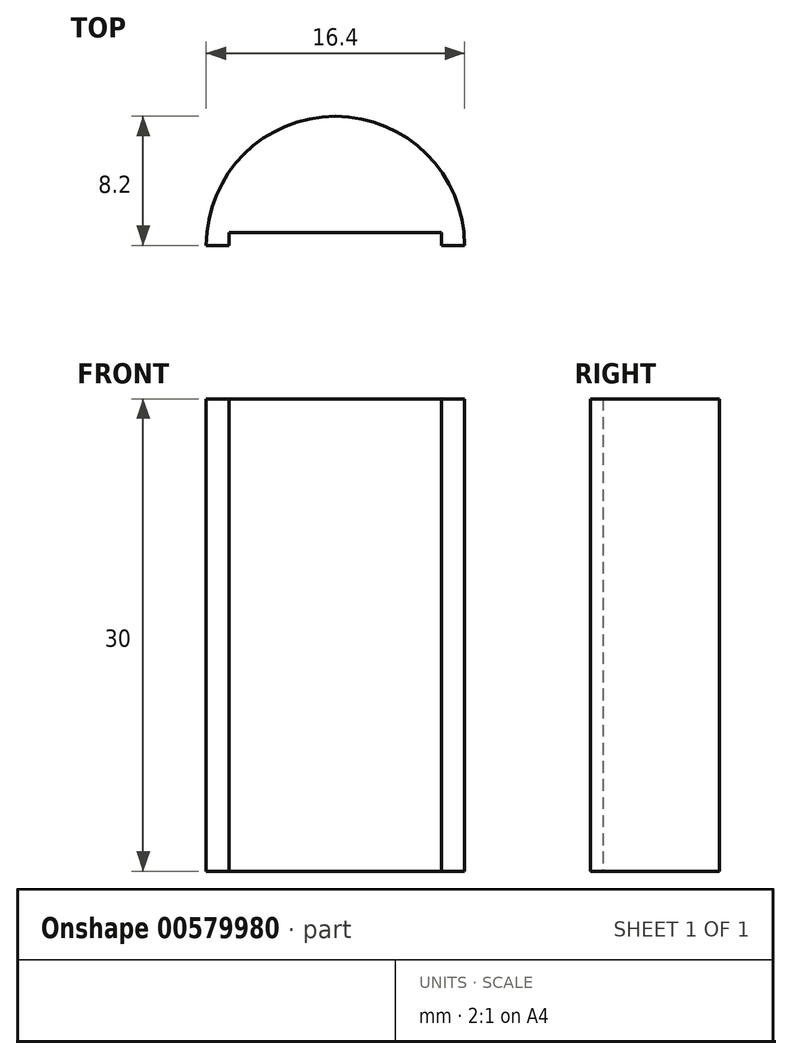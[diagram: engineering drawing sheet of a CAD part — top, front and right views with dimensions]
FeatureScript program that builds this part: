
annotation { "Feature Type Name" : "Feature", "Feature Type Description" : "" }
export const myFeature = defineFeature(function(context is Context, id is Id, definition is map)
    precondition{}
    {
        {
            var Q0;
            Q0=qCreatedBy(makeId("Top.planeOp"),FACE);
            var sketch = newSketch(context, id + "F0", { "sketchPlane" : qUnion([Q0])});
            skArc(sketch, "E0", {"start": v(-8.2, 0) * mm, "mid": v(0, 8.2) * mm, "end": v(8.2, 0) * mm});
            skLineSegment(sketch, "E1", {"start": v(-8.2, 0) * mm, "end": v(-6.75, 0) * mm});
            skLineSegment(sketch, "E2", {"start": v(-6.75, 0) * mm, "end": v(-6.75, 0.8) * mm});
            skLineSegment(sketch, "E3", {"start": v(-6.75, 0.8) * mm, "end": v(6.75, 0.8) * mm});
            skLineSegment(sketch, "E4", {"start": v(6.75, 0.8) * mm, "end": v(6.75, 0) * mm});
            skLineSegment(sketch, "E5", {"start": v(6.75, 0) * mm, "end": v(8.2, 0) * mm});
            skSolve(sketch);
        }
        {
            var Q0;
            Q0 = qSketchRegion(id + "F0", true);
            extrude(context, id + "F1", {"entities" : qUnion([Q0]), "depth" : 30 * mm, "offsetDistance" : 25 * mm});
        }
    });
